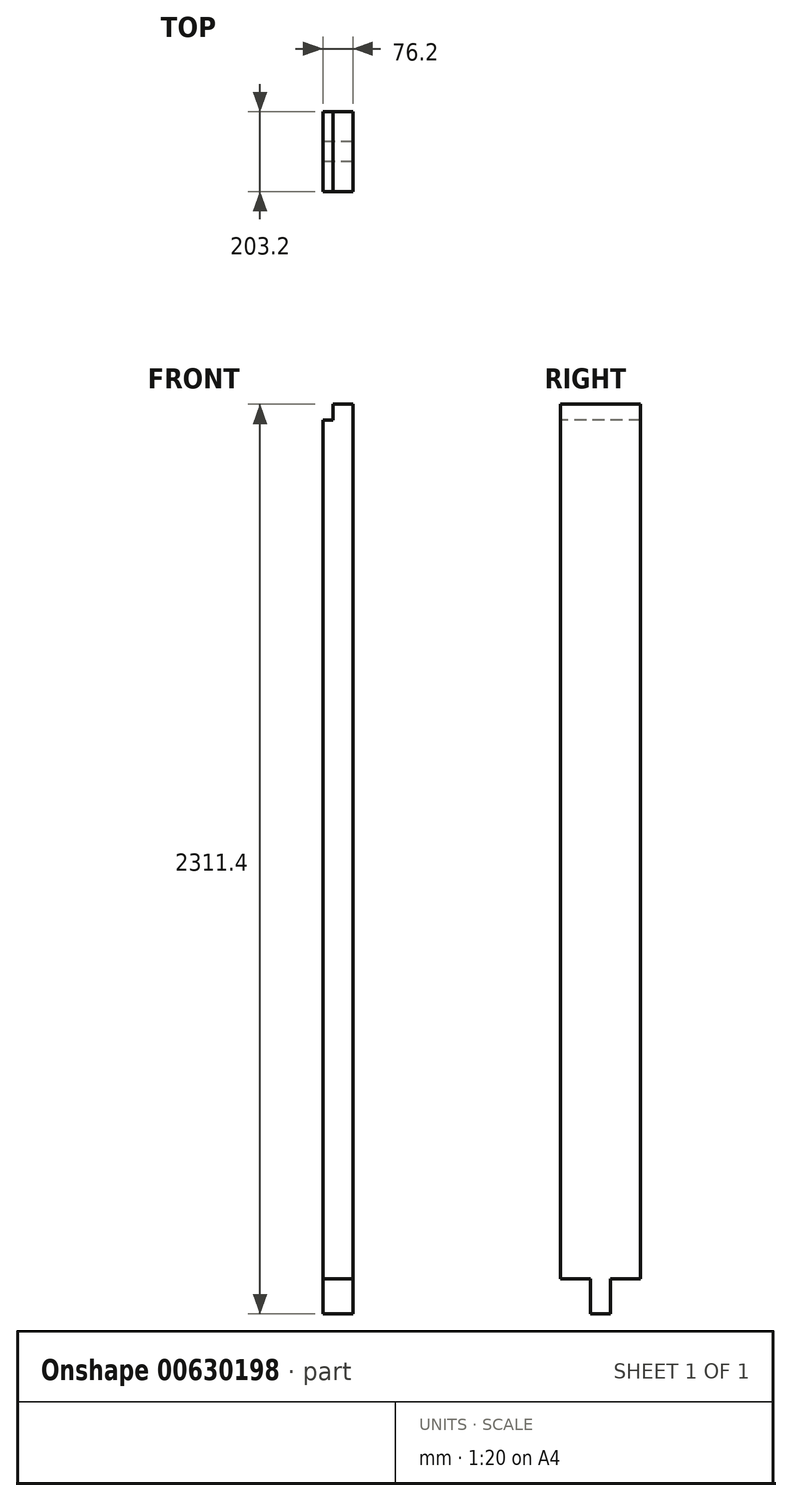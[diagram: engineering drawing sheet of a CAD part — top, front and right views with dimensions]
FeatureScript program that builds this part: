
annotation { "Feature Type Name" : "Feature", "Feature Type Description" : "" }
export const myFeature = defineFeature(function(context is Context, id is Id, definition is map)
    precondition{}
    {
        {
            var Q0;
            Q0=qCreatedBy(makeId("Right.planeOp"),FACE);
            var sketch = newSketch(context, id + "F0", { "sketchPlane" : qUnion([Q0])});
            skLineSegment(sketch, "E0.bottom", {"start": v(101.6, 1111.25) * mm, "end": v(-101.6, 1111.25) * mm});
            skLineSegment(sketch, "E0.top", {"start": v(101.6, -1111.25) * mm, "end": v(-101.6, -1111.25) * mm});
            skLineSegment(sketch, "E0.left", {"start": v(101.6, 1111.25) * mm, "end": v(101.6, -1111.25) * mm});
            skLineSegment(sketch, "E0.right", {"start": v(-101.6, 1111.25) * mm, "end": v(-101.6, -1111.25) * mm});
            skPoint(sketch, "E0.middle", {"position": v(0, 0) * mm});
            skLineSegment(sketch, "E1.bottom", {"start": v(25.4, -1200.15) * mm, "end": v(-25.4, -1200.15) * mm});
            skLineSegment(sketch, "E1.top", {"start": v(25.4, -1022.35) * mm, "end": v(-25.4, -1022.35) * mm});
            skLineSegment(sketch, "E1.left", {"start": v(25.4, -1200.15) * mm, "end": v(25.4, -1022.35) * mm});
            skLineSegment(sketch, "E1.right", {"start": v(-25.4, -1200.15) * mm, "end": v(-25.4, -1022.35) * mm});
            skPoint(sketch, "E1.middle", {"position": v(0, -1111.25) * mm});
            skSolve(sketch);
        }
        {
            var Q0;
            Q0=qSketchRegion(id+"F0",true);
            extrude(context, id + "F1", {"entities" : qUnion([Q0]), "depth" : 76.2 * mm, "offsetDistance" : 25.4 * mm});
        }
        {
            var Q0;
            Q0=makeQuery(id+"F1.opExtrude","SWEPT_FACE",FACE,{"disambiguationData":[OSD([sQuery(id+"F0.wireOp",EDGE,"E0.right")])]});
            var sketch = newSketch(context, id + "F2", { "sketchPlane" : qUnion([Q0])});
            skLineSegment(sketch, "E2", {"start": v(0, 1070.5) * mm, "end": v(25.4, 1070.5) * mm});
            skLineSegment(sketch, "E3", {"start": v(25.4, 1070.5) * mm, "end": v(25.4, 1111.25) * mm});
            skSolve(sketch);
        }
        {
            var Q0;
            {var subQ0=sQuery(id+"F2.wireOp",EDGE,"E2");Q0=makeQuery(id+"F2.imprint","IMPRINT",FACE,{"disambiguationData":[TD([[makeQuery(id+"F2.imprint","IMPRINT",EDGE,{"derivedFrom":subQ0}),1.0]])]});}
            extrude(context, id + "F3", {"entities" : qUnion([Q0]), "operationType" : NewBodyOperationType.REMOVE, "oppositeDirection" : true, "depth" : 203.2 * mm, "offsetDistance" : 25.4 * mm});
        }
    });
